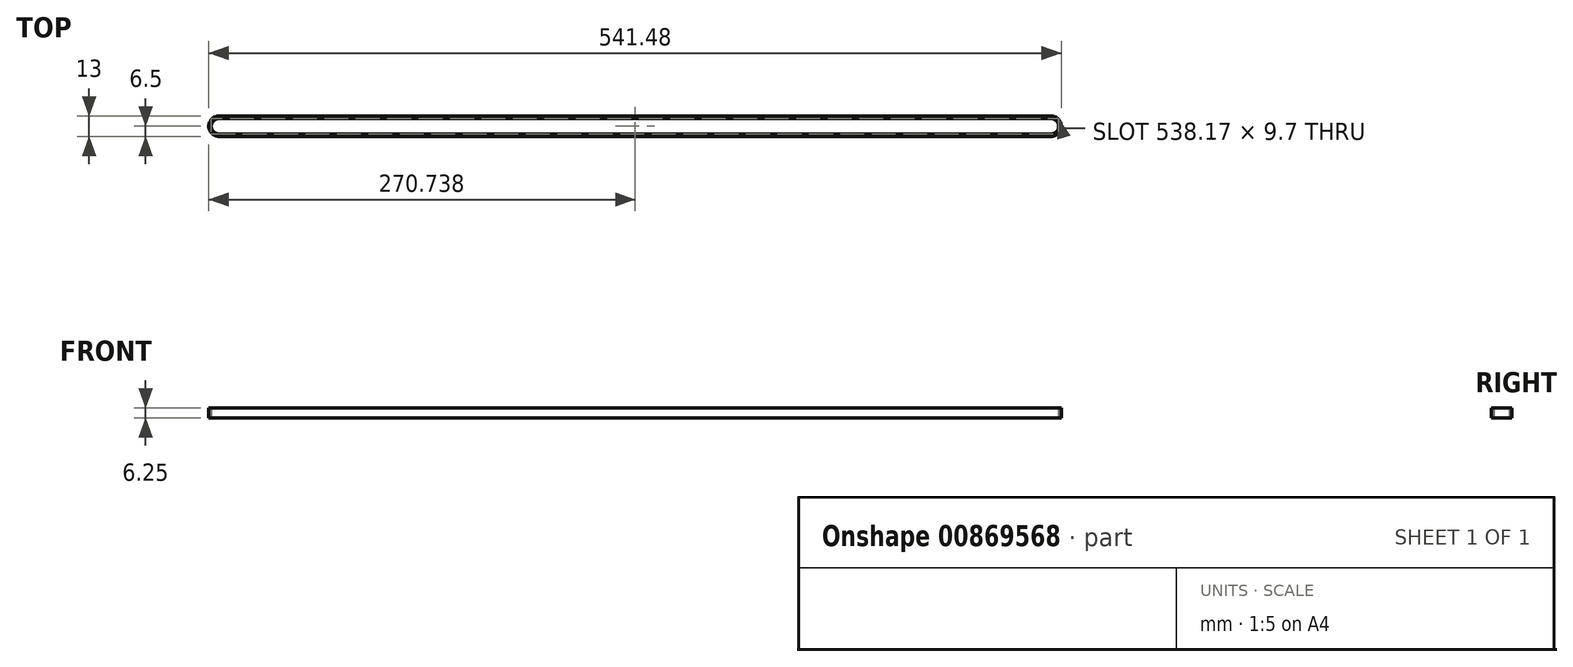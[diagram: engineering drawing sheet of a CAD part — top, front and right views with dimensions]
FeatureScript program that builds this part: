
annotation { "Feature Type Name" : "Feature", "Feature Type Description" : "" }
export const myFeature = defineFeature(function(context is Context, id is Id, definition is map)
    precondition{}
    {
        {
            var Q0;
            Q0=qCreatedBy(makeId("Top.planeOp"),FACE);
            var sketch = newSketch(context, id + "F0", { "sketchPlane" : qUnion([Q0])});
            skArc(sketch, "E0", {"start": v(0, 4.85) * mm, "mid": v(-4.85, 0) * mm, "end": v(0, -4.85) * mm});
            skArc(sketch, "E1", {"start": v(0, 6.5) * mm, "mid": v(-6.5, 0) * mm, "end": v(0, -6.5) * mm});
            skArc(sketch, "E2", {"start": v(528.48, -6.5) * mm, "mid": v(534.98, 0) * mm, "end": v(528.48, 6.5) * mm});
            skArc(sketch, "E3", {"start": v(528.48, -4.85) * mm, "mid": v(533.32, 0) * mm, "end": v(528.48, 4.85) * mm});
            skLineSegment(sketch, "E4", {"start": v(0, 4.85) * mm, "end": v(528.48, 4.85) * mm});
            skLineSegment(sketch, "E5", {"start": v(0, -4.85) * mm, "end": v(528.48, -4.85) * mm});
            skLineSegment(sketch, "E6", {"start": v(0, 6.5) * mm, "end": v(528.48, 6.5) * mm});
            skLineSegment(sketch, "E7", {"start": v(0, -6.5) * mm, "end": v(528.48, -6.5) * mm});
            skSolve(sketch);
        }
        {
            var Q0;
            Q0 = qSketchRegion(id + "F0", true);
            extrude(context, id + "F1", {"entities" : qUnion([Q0]), "depth" : 6.25 * mm, "offsetDistance" : 25 * mm});
        }
    });
